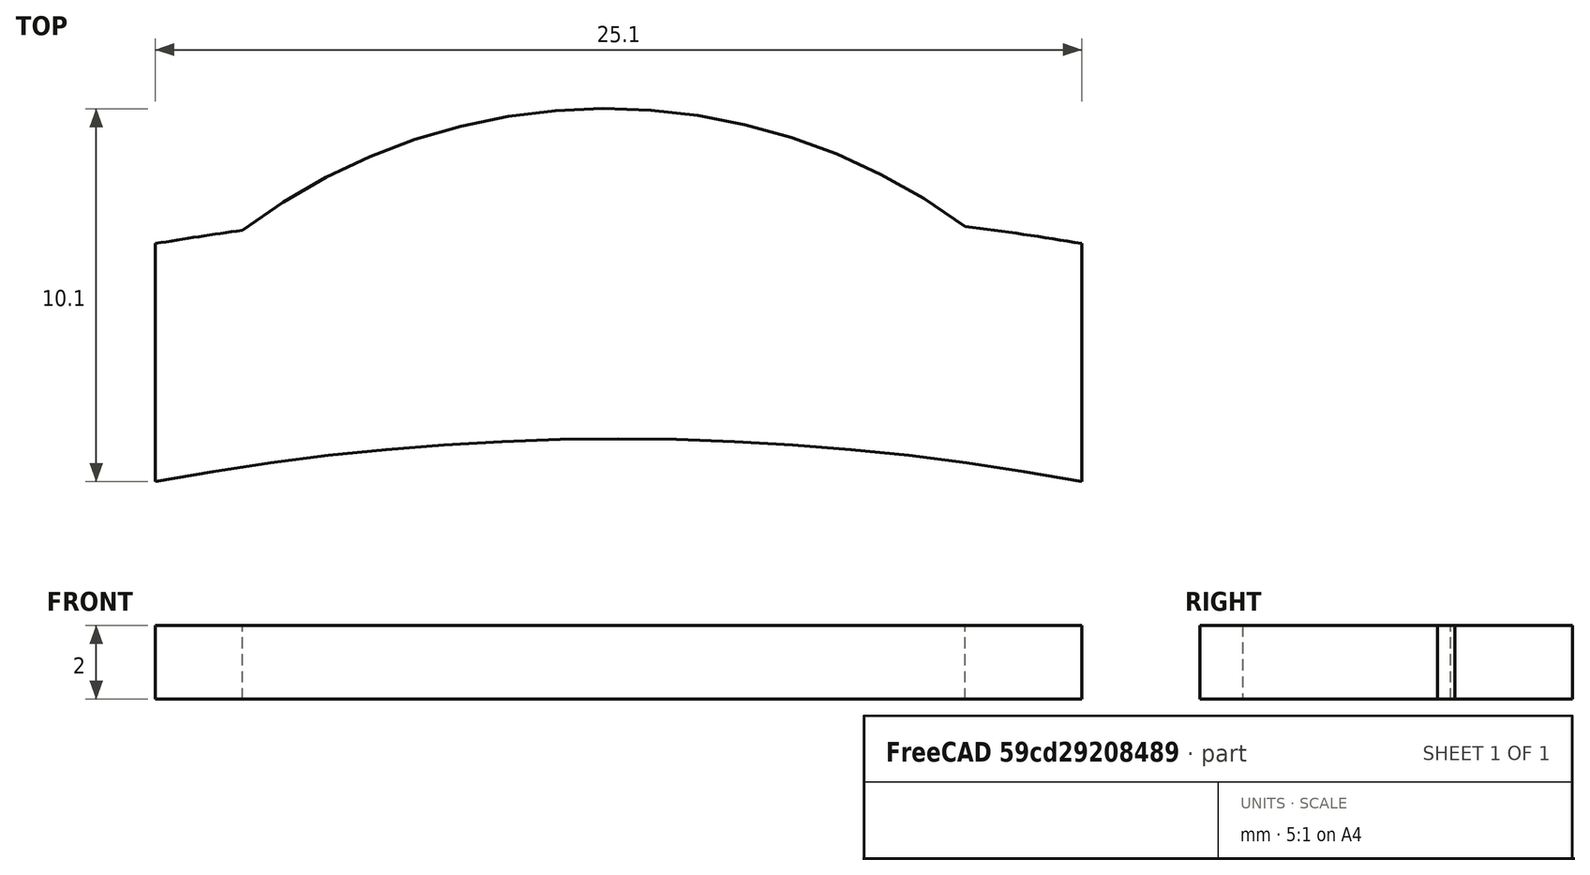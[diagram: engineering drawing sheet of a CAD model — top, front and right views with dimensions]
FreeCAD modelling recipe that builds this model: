
FCSTD DOCUMENT  (FreeCAD 0.22R37841 (Git))
Label: GuardaAfeitadora
License: All rights reserved
LicenseURL: http://en.wikipedia.org/wiki/All_rights_reserved
objects: Sketcher::SketchObject×1, PartDesign::Pad×1, PartDesign::Body×1
note: 4 computed .brp shape members not serialized (recipe doc carries the construction recipe); baked Part::Feature solids carry a one-line shape summary decoded from their .brp

FEATURE [Sketcher::SketchObject] Sketch
  AttachmentSupport = -> [XY_Plane]
  FullyConstrained = false
  MapMode = 5
  sketch-geometry (6):
    g0: ArcOfCircle CenterX=12.55 CenterY=-50 CenterZ=0 NormalX=0 NormalY=0 NormalZ=1 AngleXU=0 Radius=68.7551 StartAngle=1.38724 EndAngle=1.75436
    g1: ArcOfCircle CenterX=12.55 CenterY=-50 CenterZ=0 NormalX=0 NormalY=0 NormalZ=1 AngleXU=0 Radius=75.1 StartAngle=1.4029 EndAngle=1.4454
    g2: ArcOfCircle CenterX=12.2199 CenterY=11.3037 CenterZ=0 NormalX=0 NormalY=0 NormalZ=1 AngleXU=0 Radius=16.3997 StartAngle=0.936182 EndAngle=2.21618
    g3: ArcOfCircle CenterX=12.55 CenterY=-50 CenterZ=0 NormalX=0 NormalY=0 NormalZ=1 AngleXU=0 Radius=75.1 StartAngle=1.70696 EndAngle=1.73869
    g4: LineSegment StartX=-1.8e-15 StartY=24.044 StartZ=0 EndX=-1.8e-15 EndY=17.6 EndZ=0
    g5: LineSegment StartX=25.1 StartY=24.044 StartZ=0 EndX=25.1 EndY=17.6 EndZ=0
  constraints (11):
    c: Coincident(g1,g0)
    c: Equal(g1,g3)
    c: Coincident(g1,g2)
    c: Coincident(g3,g2)
    c: Coincident(g1,g3)
    c: Coincident(g4,g3)
    c: Coincident(g4,g0)
    c: Vertical(g4)
    c: Coincident(g5,g1)
    c: Coincident(g5,g0)
    c: Vertical(g5)
FEATURE [PartDesign::Pad] Pad
  Direction = (0,0,1)
  Length = 2
  Length2 = 10
  Profile = -> Sketch
  ReferenceAxis = -> Sketch [N_Axis]
  Suppressed = false
  Type = 0
FEATURE [PartDesign::Body] Body
  AllowCompound = false
  Group = -> [Sketch,Pad]
  Origin = -> Origin
  Tip = -> Pad
